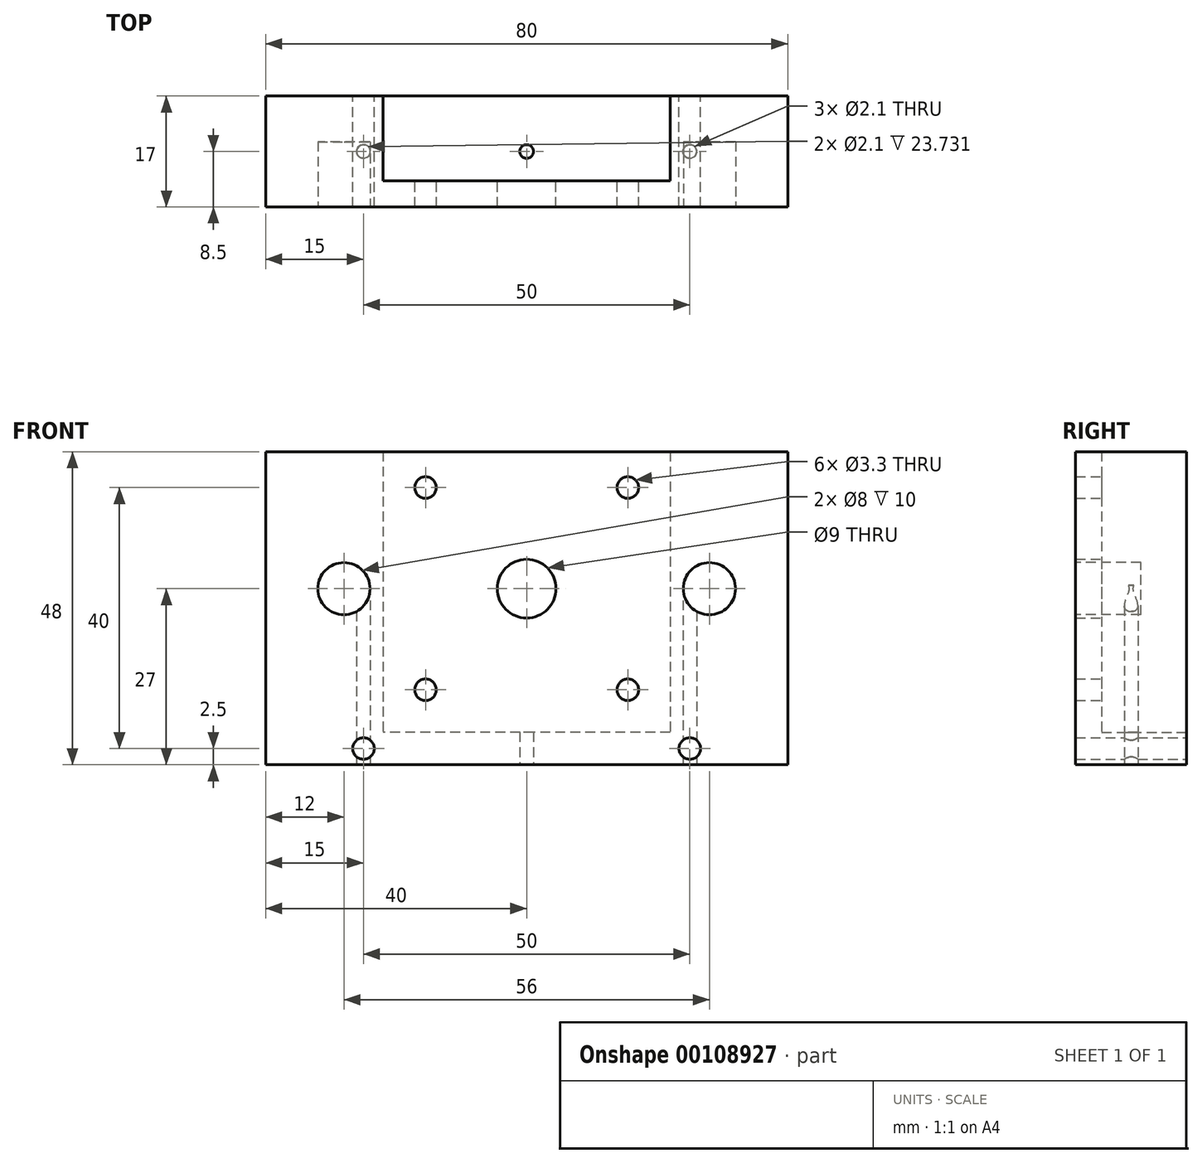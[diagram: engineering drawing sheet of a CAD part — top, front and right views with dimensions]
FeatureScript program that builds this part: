
annotation { "Feature Type Name" : "Feature", "Feature Type Description" : "" }
export const myFeature = defineFeature(function(context is Context, id is Id, definition is map)
    precondition{}
    {
        {
            var Q0;
            Q0=qCreatedBy(makeId("Top.planeOp"),FACE);
            var sketch = newSketch(context, id + "F0", { "sketchPlane" : qUnion([Q0])});
            skLineSegment(sketch, "E0.bottom", {"start": v(40, -8.5) * mm, "end": v(-40, -8.5) * mm});
            skLineSegment(sketch, "E0.top", {"start": v(40, 8.5) * mm, "end": v(-40, 8.5) * mm});
            skLineSegment(sketch, "E0.left", {"start": v(40, -8.5) * mm, "end": v(40, 8.5) * mm});
            skLineSegment(sketch, "E0.right", {"start": v(-40, -8.5) * mm, "end": v(-40, 8.5) * mm});
            skPoint(sketch, "E0.middle", {"position": v(0, 0) * mm});
            skLineSegment(sketch, "E1", {"start": v(0, 0) * mm, "end": v(-25, 0) * mm, "construction": true});
            skLineSegment(sketch, "E2", {"start": v(0, 0) * mm, "end": v(25, 0) * mm, "construction": true});
            skPoint(sketch, "E3", {"position": v(-25, 0) * mm});
            skPoint(sketch, "E4", {"position": v(25, 0) * mm});
            skCircle(sketch, "E5", {"center": v(25, 0) * mm, "radius": 1.05 * mm});
            skCircle(sketch, "E6", {"center": v(0, 0) * mm, "radius": 1.05 * mm});
            skCircle(sketch, "E7", {"center": v(-25, 0) * mm, "radius": 1.05 * mm});
            skSolve(sketch);
        }
        {
            var Q0;
            Q0 = qSketchRegion(id + "F0", true);
            extrude(context, id + "F1", {"entities" : qUnion([Q0]), "endBound" : BoundingType.SYMMETRIC, "depth" : 5 * mm});
        }
        {
            var Q0;
            Q0=makeQuery(id+"F1.opExtrude","CAP_FACE",FACE,{"disambiguationData":[OSD([sQuery(id+"F0.wireOp",EDGE,"E0.bottom"),sQuery(id+"F0.wireOp",EDGE,"E0.top"),sQuery(id+"F0.wireOp",EDGE,"E0.left"),sQuery(id+"F0.wireOp",EDGE,"E0.right")])],"isStart":false});
            var sketch = newSketch(context, id + "F2", { "sketchPlane" : qUnion([Q0])});
            skLineSegment(sketch, "E8.bottom", {"start": v(40, -8.5) * mm, "end": v(-40, -8.5) * mm});
            skLineSegment(sketch, "E8.top", {"start": v(40, 8.5) * mm, "end": v(22, 8.5) * mm});
            skLineSegment(sketch, "E8.left", {"start": v(40, -8.5) * mm, "end": v(40, 8.5) * mm});
            skLineSegment(sketch, "E8.right", {"start": v(-40, -8.5) * mm, "end": v(-40, 8.5) * mm});
            skLineSegment(sketch, "E9.bottom", {"start": v(22, -4.5) * mm, "end": v(-22, -4.5) * mm});
            skLineSegment(sketch, "E9.left", {"start": v(22, -4.5) * mm, "end": v(22, 8.5) * mm});
            skLineSegment(sketch, "E9.right", {"start": v(-22, -4.5) * mm, "end": v(-22, 8.5) * mm});
            skLineSegment(sketch, "E10.trimOffspring", {"start": v(-22, 8.5) * mm, "end": v(-40, 8.5) * mm});
            skPoint(sketch, "E11", {"position": v(0, -4.5) * mm});
            skLineSegment(sketch, "E12", {"start": v(0, -8.5) * mm, "end": v(0, 8.5) * mm, "construction": true});
            skSolve(sketch);
        }
        {
            var Q0;
            Q0 = qSketchRegion(id + "F2", true);
            var Q1;
            Q1=makeQuery(id+"F2.imprint","IMPRINT",FACE,{"disambiguationData":[TD([[makeQuery(id+"F2.imprint","IMPRINT",EDGE,{"derivedFrom":sQuery(id+"F2.wireOp",EDGE,"wSEDSmoU-HDEk-zv8Z-Yyo2-8jmHmdKh1jkQ.bottom")}),1.0]])]});
            extrude(context, id + "F3", {"entities" : qUnion([Q0, Q1]), "operationType" : NewBodyOperationType.ADD, "depth" : 43 * mm});
        }
        {
            var Q0;
            Q0=makeQuery(id+"F3.opExtrude","SWEPT_FACE",FACE,{"disambiguationData":[OSD([sQuery(id+"F2.wireOp",EDGE,"E9.bottom")])]});
            var sketch = newSketch(context, id + "F4", { "sketchPlane" : qUnion([Q0])});
            skLineSegment(sketch, "E13.bottom", {"start": v(-15.5, 40) * mm, "end": v(15.5, 40) * mm, "construction": true});
            skLineSegment(sketch, "E13.top", {"start": v(-15.5, 9) * mm, "end": v(15.5, 9) * mm, "construction": true});
            skLineSegment(sketch, "E13.left", {"start": v(-15.5, 40) * mm, "end": v(-15.5, 9) * mm, "construction": true});
            skLineSegment(sketch, "E13.right", {"start": v(15.5, 40) * mm, "end": v(15.5, 9) * mm, "construction": true});
            skLineSegment(sketch, "E14", {"start": v(-15.5, 40) * mm, "end": v(15.5, 9) * mm, "construction": true});
            skLineSegment(sketch, "E15", {"start": v(15.5, 40) * mm, "end": v(-15.5, 9) * mm, "construction": true});
            skPoint(sketch, "E16", {"position": v(0, 24.5) * mm});
            skCircle(sketch, "E17", {"center": v(0, 24.5) * mm, "radius": 4.5 * mm});
            skSolve(sketch);
        }
        {
            var Q0;
            Q0=makeQuery(id+"F0.imprint","IMPRINT",FACE,{"disambiguationData":[TD([[makeQuery(id+"F0.imprint","IMPRINT",EDGE,{"derivedFrom":sQuery(id+"F0.wireOp",EDGE,"E7")}),1.0]])]});
            var Q1;
            Q1=makeQuery(id+"F0.imprint","IMPRINT",FACE,{"disambiguationData":[TD([[makeQuery(id+"F0.imprint","IMPRINT",EDGE,{"derivedFrom":sQuery(id+"F0.wireOp",EDGE,"E6")}),1.0]])]});
            var Q2;
            Q2=makeQuery(id+"F0.imprint","IMPRINT",FACE,{"disambiguationData":[TD([[makeQuery(id+"F0.imprint","IMPRINT",EDGE,{"derivedFrom":sQuery(id+"F0.wireOp",EDGE,"E5")}),1.0]])]});
            extrude(context, id + "F5", {"entities" : qUnion([Q0, Q1, Q2]), "operationType" : NewBodyOperationType.REMOVE, "depth" : 25 * mm});
        }
        {
            var Q0;
            Q0=makeQuery(id+"F3.boolean.opBoolean","MERGE",FACE,{"derivedFrom":[makeQuery(id+"F1.opExtrude","SWEPT_FACE",FACE,{"disambiguationData":[OSD([sQuery(id+"F0.wireOp",EDGE,"E0.top")])]}),makeQuery(id+"F3.opExtrude","SWEPT_FACE",FACE,{"disambiguationData":[OSD([sQuery(id+"F2.wireOp",EDGE,"E8.top")])]}),makeQuery(id+"F3.opExtrude","SWEPT_FACE",FACE,{"disambiguationData":[OSD([sQuery(id+"F2.wireOp",EDGE,"E10.trimOffspring")])]})]});
            var sketch = newSketch(context, id + "F6", { "sketchPlane" : qUnion([Q0])});
            skPoint(sketch, "E18.0", {"position": v(25, 0) * mm});
            skPoint(sketch, "E19.0", {"position": v(-25, 0) * mm});
            skSolve(sketch);
        }
        {
            var Q0;
            Q0=sQuery(id+"F6.wireOp",VERTEX,"E18.0");
            var Q1;
            Q1=sQuery(id+"F6.wireOp",VERTEX,"E19.0");
            var Q2;
            Q2=makeQuery(id+"F1.opExtrude","SWEPT_BODY",BODY,{"disambiguationData":[OSD([sQuery(id+"F0.wireOp",EDGE,"E0.bottom"),sQuery(id+"F0.wireOp",EDGE,"E0.top"),sQuery(id+"F0.wireOp",EDGE,"E0.left"),sQuery(id+"F0.wireOp",EDGE,"E0.right"),sQuery(id+"F0.wireOp",EDGE,"E5"),sQuery(id+"F0.wireOp",EDGE,"E6"),sQuery(id+"F0.wireOp",EDGE,"E7")])]});
            hole(context, id + "F7", {"style" : HoleStyle.SIMPLE, "endStyle" : HoleEndStyle.THROUGH, "standardTappedOrClearance" : lookupTablePath({ "standard" : "ISO", "fit" : "Normal", "size" : "M3", "type" : "Clearance" }), "standardBlindInLast" : lookupTablePath({ "fit" : "Standard", "standard" : "ISO", "size" : "M3", "type" : "Clearance" }), "holeDiameter" : 3.3 * mm, "locations" : qUnion([Q0, Q1]), "scope" : qUnion([Q2]), "isTappedThrough" : true});
        }
        {
            var Q0;
            Q0=sQuery(id+"F4.wireOp",VERTEX,"E13.right.start");
            var Q1;
            Q1=sQuery(id+"F4.wireOp",VERTEX,"E13.left.start");
            var Q2;
            Q2=sQuery(id+"F4.wireOp",VERTEX,"E13.left.end");
            var Q3;
            Q3=sQuery(id+"F4.wireOp",VERTEX,"E13.right.end");
            var Q4;
            Q4=makeQuery(id+"F1.opExtrude","SWEPT_BODY",BODY,{"disambiguationData":[OSD([sQuery(id+"F0.wireOp",EDGE,"E0.bottom"),sQuery(id+"F0.wireOp",EDGE,"E0.top"),sQuery(id+"F0.wireOp",EDGE,"E0.left"),sQuery(id+"F0.wireOp",EDGE,"E0.right"),sQuery(id+"F0.wireOp",EDGE,"E5"),sQuery(id+"F0.wireOp",EDGE,"E6"),sQuery(id+"F0.wireOp",EDGE,"E7")])]});
            hole(context, id + "F8", {"style" : HoleStyle.SIMPLE, "endStyle" : HoleEndStyle.THROUGH, "standardTappedOrClearance" : lookupTablePath({ "standard" : "ISO", "fit" : "Normal", "size" : "M3", "type" : "Clearance" }), "standardBlindInLast" : lookupTablePath({ "fit" : "Standard", "standard" : "ISO", "size" : "M3", "type" : "Clearance" }), "holeDiameter" : 3.3 * mm, "locations" : qUnion([Q0, Q1, Q2, Q3]), "scope" : qUnion([Q4]), "isTappedThrough" : true});
        }
        {
            var Q0;
            Q0=makeQuery(id+"F4.imprint","IMPRINT",FACE,{"disambiguationData":[TD([[makeQuery(id+"F4.imprint","IMPRINT",EDGE,{"derivedFrom":sQuery(id+"F4.wireOp",EDGE,"E17")}),1.0]])]});
            var Q1;
            Q1=sQuery(id+"F4.wireOp",EDGE,"E17");
            extrude(context, id + "F9", {"entities" : qUnion([Q0]), "operationType" : NewBodyOperationType.REMOVE, "surfaceEntities" : qUnion([Q1]), "endBound" : BoundingType.THROUGH_ALL, "oppositeDirection" : true, "depth" : 25 * mm});
        }
        {
            var Q0;
            Q0=makeQuery(id+"F3.boolean.opBoolean","MERGE",FACE,{"derivedFrom":[makeQuery(id+"F1.opExtrude","SWEPT_FACE",FACE,{"disambiguationData":[OSD([sQuery(id+"F0.wireOp",EDGE,"E0.bottom")])]}),makeQuery(id+"F3.opExtrude","SWEPT_FACE",FACE,{"disambiguationData":[OSD([sQuery(id+"F2.wireOp",EDGE,"wSEDSmoU-HDEk-zv8Z-Yyo2-8jmHmdKh1jkQ.top"),sQuery(id+"F2.wireOp",EDGE,"7cbcb2f8-9b66-4ae1-b311-715de91a1cf00.MirrorCS"),sQuery(id+"F2.wireOp",EDGE,"P8m8yoBS-wXvZ-HwUU-XP83-H87GxBExd7wv.bottom")])]})]});
            var sketch = newSketch(context, id + "F10", { "sketchPlane" : qUnion([Q0])});
            skLineSegment(sketch, "E20", {"start": v(0, 24.5) * mm, "end": v(-28, 24.5) * mm, "construction": true});
            skLineSegment(sketch, "E21", {"start": v(0, 24.5) * mm, "end": v(28, 24.5) * mm, "construction": true});
            skCircle(sketch, "E22", {"center": v(-28, 24.5) * mm, "radius": 4 * mm});
            skCircle(sketch, "E23.MirrorC", {"center": v(28, 24.5) * mm, "radius": 4 * mm});
            skSolve(sketch);
        }
        {
            var Q0;
            Q0 = qSketchRegion(id + "F10", true);
            extrude(context, id + "F11", {"entities" : qUnion([Q0]), "operationType" : NewBodyOperationType.REMOVE, "oppositeDirection" : true, "depth" : 10 * mm});
        }
    });
